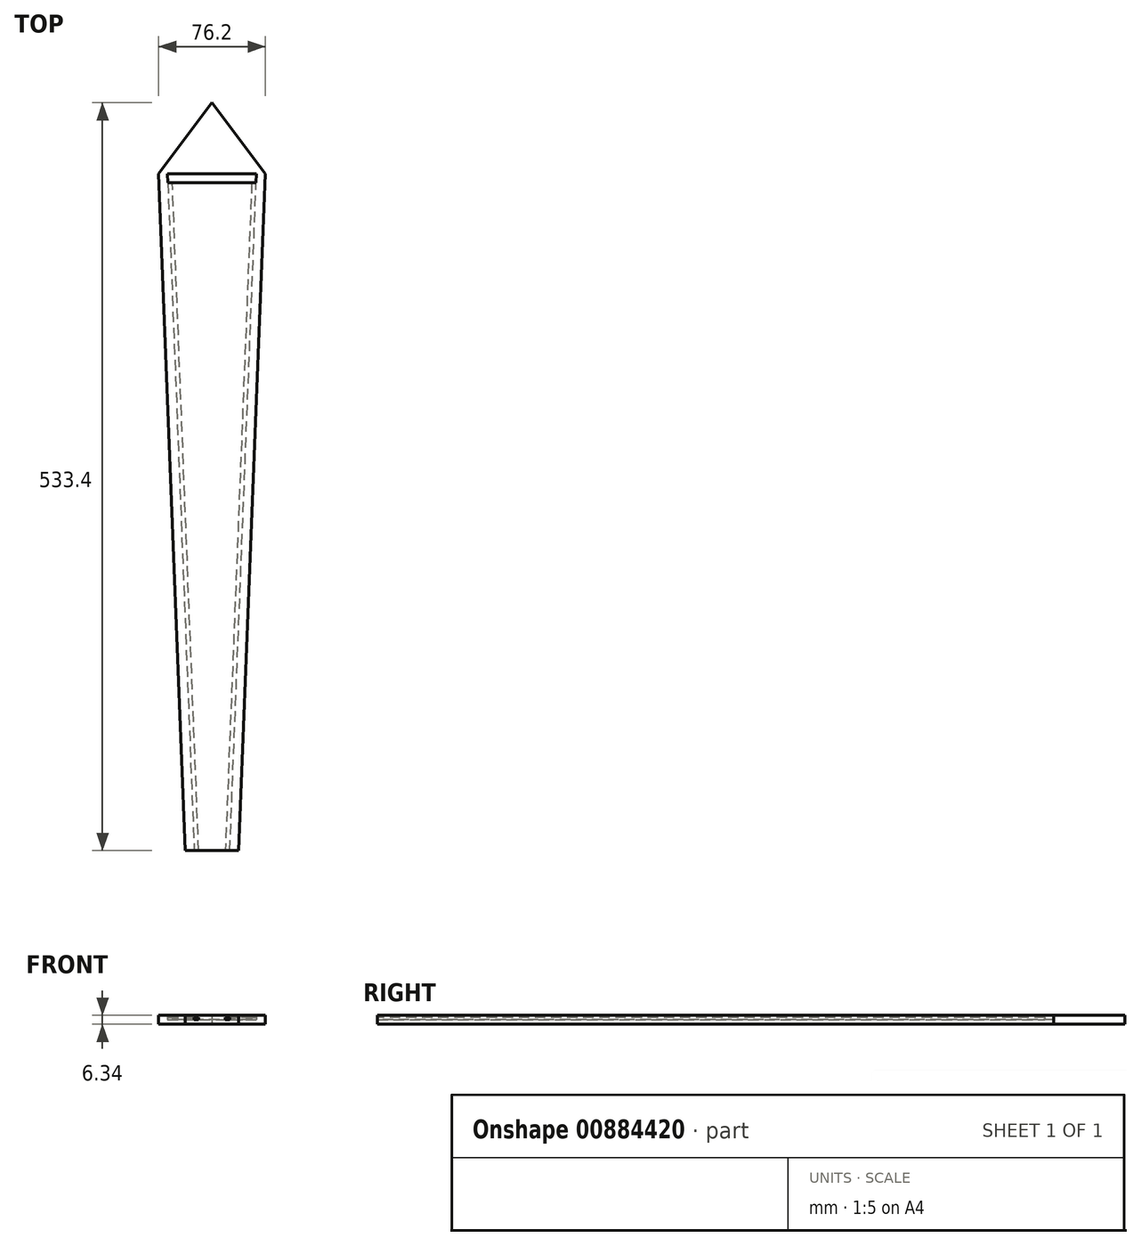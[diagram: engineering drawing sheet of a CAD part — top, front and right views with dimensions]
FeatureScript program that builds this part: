
annotation { "Feature Type Name" : "Feature", "Feature Type Description" : "" }
export const myFeature = defineFeature(function(context is Context, id is Id, definition is map)
    precondition{}
    {
        {
            var Q0;
            Q0=qCreatedBy(makeId("Top.planeOp"),FACE);
            var sketch = newSketch(context, id + "F0", { "sketchPlane" : qUnion([Q0])});
            skLineSegment(sketch, "E0", {"start": v(-38.1, 215.9) * mm, "end": v(0, 266.7) * mm});
            skLineSegment(sketch, "E1", {"start": v(0, 266.7) * mm, "end": v(38.1, 215.9) * mm});
            skLineSegment(sketch, "E2", {"start": v(38.1, 215.9) * mm, "end": v(19.05, -266.7) * mm});
            skLineSegment(sketch, "E3", {"start": v(19.05, -266.7) * mm, "end": v(-19.05, -266.7) * mm});
            skLineSegment(sketch, "E4", {"start": v(-19.05, -266.7) * mm, "end": v(-38.1, 215.9) * mm});
            skSolve(sketch);
        }
        {
            var Q0;
            Q0 = qSketchRegion(id + "F0", true);
            extrude(context, id + "F1", {"entities" : qUnion([Q0]), "depth" : 3.17 * mm, "offsetDistance" : 25.4 * mm});
        }
        {
            var Q0;
            Q0=qCreatedBy(makeId("Top.planeOp"),FACE);
            var sketch = newSketch(context, id + "F2", { "sketchPlane" : qUnion([Q0])});
            skLineSegment(sketch, "E5", {"start": v(-31.75, 215.9) * mm, "end": v(-12.69, -266.95) * mm});
            skLineSegment(sketch, "E6", {"start": v(-31.75, 215.9) * mm, "end": v(31.75, 215.9) * mm});
            skLineSegment(sketch, "E7", {"start": v(12.7, -266.83) * mm, "end": v(31.75, 215.9) * mm});
            skLineSegment(sketch, "E8", {"start": v(12.7, -266.83) * mm, "end": v(9.52, -266.7) * mm});
            skLineSegment(sketch, "E9", {"start": v(28.32, 209.55) * mm, "end": v(9.52, -266.7) * mm});
            skLineSegment(sketch, "E10", {"start": v(28.32, 209.55) * mm, "end": v(-28.32, 209.55) * mm});
            skLineSegment(sketch, "E11", {"start": v(-9.51, -266.83) * mm, "end": v(-28.32, 209.55) * mm});
            skLineSegment(sketch, "E12", {"start": v(-9.51, -266.83) * mm, "end": v(-12.69, -266.95) * mm});
            skSolve(sketch);
        }
        {
            var Q0;
            Q0=makeQuery(id+"F2.imprint","IMPRINT",FACE,{"disambiguationData":[TD([[makeQuery(id+"F2.imprint","IMPRINT",EDGE,{"derivedFrom":sQuery(id+"F2.wireOp",EDGE,"E5")}),1.0]])]});
            extrude(context, id + "F3", {"entities" : qUnion([Q0]), "operationType" : NewBodyOperationType.REMOVE, "depth" : 1.59 * mm, "offsetDistance" : 25.4 * mm});
        }
        {
            var Q0;
            Q0=makeQuery(id+"F1.opExtrude","CAP_FACE",FACE,{"disambiguationData":[OSD([sQuery(id+"F0.wireOp",EDGE,"E0"),sQuery(id+"F0.wireOp",EDGE,"E1"),sQuery(id+"F0.wireOp",EDGE,"E2"),sQuery(id+"F0.wireOp",EDGE,"E3"),sQuery(id+"F0.wireOp",EDGE,"E4")])],"isStart":false});
            var sketch = newSketch(context, id + "F4", { "sketchPlane" : qUnion([Q0])});
            skLineSegment(sketch, "E13", {"start": v(-31.75, 215.9) * mm, "end": v(-31.5, 209.55) * mm});
            skLineSegment(sketch, "E14", {"start": v(-31.5, 209.55) * mm, "end": v(31.5, 209.55) * mm});
            skLineSegment(sketch, "E15", {"start": v(31.5, 209.55) * mm, "end": v(31.75, 215.9) * mm});
            skLineSegment(sketch, "E16", {"start": v(31.75, 215.9) * mm, "end": v(-31.75, 215.9) * mm});
            skSolve(sketch);
        }
        {
            var Q0;
            Q0 = qSketchRegion(id + "F4", true);
            extrude(context, id + "F5", {"entities" : qUnion([Q0]), "operationType" : NewBodyOperationType.REMOVE, "oppositeDirection" : true, "depth" : 3.17 * mm, "offsetDistance" : 25.4 * mm});
        }
        {
            var Q0;
            {var subQ0=sQuery(id+"F0.wireOp",EDGE,"E2");var subQ1=sQuery(id+"F0.wireOp",EDGE,"E1");var subQ2=sQuery(id+"F0.wireOp",EDGE,"E3");var subQ3=sQuery(id+"F0.wireOp",EDGE,"E0");var subQ4=sQuery(id+"F0.wireOp",EDGE,"E4");Q0=makeQuery(id+"F3.boolean.opBoolean","SPLIT",FACE,{"disambiguationData":[TD([makeQuery(id+"F1.opExtrude","SWEPT_FACE",FACE,{"disambiguationData":[OSD([subQ3])]})])],"derivedFrom":makeQuery(id+"F1.opExtrude","CAP_FACE",FACE,{"disambiguationData":[OSD([subQ3,subQ1,subQ0,subQ2,subQ4])],"isStart":true})});}
            var sketch = newSketch(context, id + "F6", { "sketchPlane" : qUnion([Q0])});
            skLineSegment(sketch, "E17", {"start": v(-38.1, -215.9) * mm, "end": v(-19.05, 266.7) * mm});
            skLineSegment(sketch, "E18", {"start": v(-19.05, 266.7) * mm, "end": v(19.05, 266.7) * mm});
            skLineSegment(sketch, "E19", {"start": v(19.05, 266.7) * mm, "end": v(38.1, -215.9) * mm});
            skLineSegment(sketch, "E20", {"start": v(38.1, -215.9) * mm, "end": v(0, -266.7) * mm});
            skLineSegment(sketch, "E21", {"start": v(0, -266.7) * mm, "end": v(-38.1, -215.9) * mm});
            skSolve(sketch);
        }
        {
            var Q0;
            Q0 = qSketchRegion(id + "F6", true);
            extrude(context, id + "F7", {"entities" : qUnion([Q0]), "operationType" : NewBodyOperationType.ADD, "depth" : 3.17 * mm, "offsetDistance" : 25.4 * mm});
        }
    });
